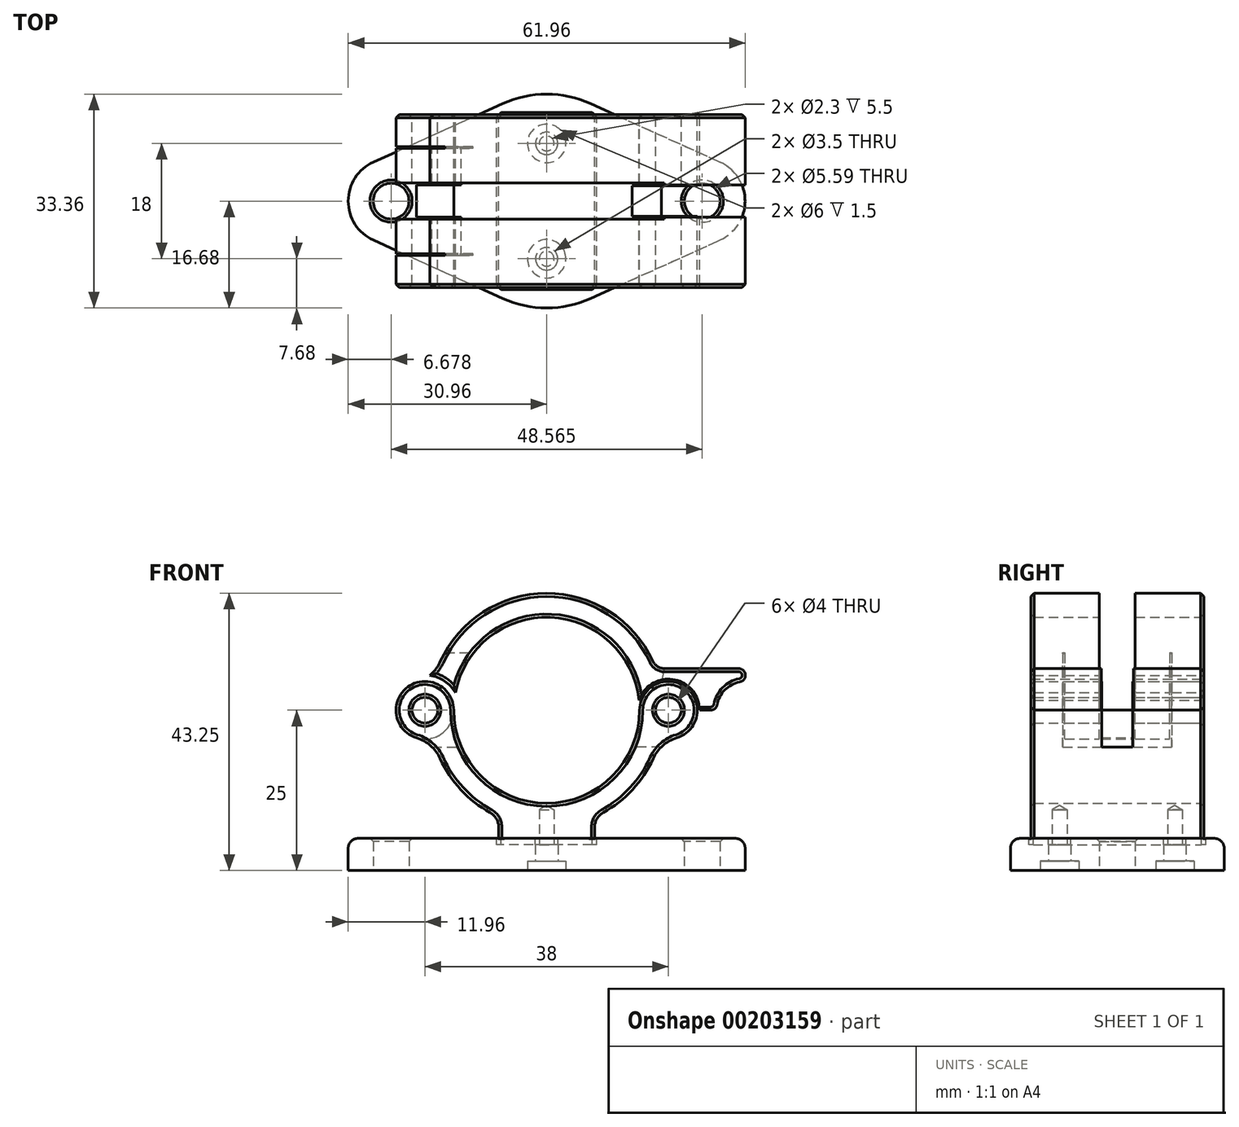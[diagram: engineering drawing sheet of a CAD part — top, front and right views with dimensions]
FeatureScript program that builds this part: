
annotation { "Feature Type Name" : "Feature", "Feature Type Description" : "" }
export const myFeature = defineFeature(function(context is Context, id is Id, definition is map)
    precondition{}
    {
        {
            var Q0;
            Q0=qCreatedBy(makeId("Top.planeOp"),FACE);
            cPlane(context, id + "F0", {"entities" : qUnion([Q0]), "cplaneType" : CPlaneType.OFFSET, "offset" : 30 * mm, "width" : 150 * mm, "height" : 150 * mm});
        }
        {
            var Q0;
            Q0=qCreatedBy(makeId("Top.planeOp"),FACE);
            cPlane(context, id + "F1", {"entities" : qUnion([Q0]), "cplaneType" : CPlaneType.OFFSET, "offset" : 4 * mm, "oppositeDirection" : true, "width" : 150 * mm, "height" : 150 * mm});
        }
        {
            var Q0;
            Q0=qCreatedBy(makeId("Front.planeOp"),FACE);
            var sketch = newSketch(context, id + "F2", { "sketchPlane" : qUnion([Q0])});
            skArc(sketch, "E0", {"start": v(14.41, 22.58) * mm, "mid": v(-14.48, 20.2) * mm, "end": v(14.5, 21) * mm});
            skArc(sketch, "E1", {"start": v(8.8, 5) * mm, "mid": v(13.39, 8.6) * mm, "end": v(16.61, 13.44) * mm});
            skLineSegment(sketch, "E2.bottom", {"start": v(7.5, 0) * mm, "end": v(-7.5, 0) * mm});
            skLineSegment(sketch, "E2.left", {"start": v(7.5, 0) * mm, "end": v(7.5, 2.82) * mm});
            skLineSegment(sketch, "E2.right", {"start": v(-7.5, 0) * mm, "end": v(-7.5, 2.82) * mm});
            skPoint(sketch, "E3.visualSharp", {"position": v(-7.5, 4.36) * mm});
            skArc(sketch, "E3.filletArc", {"start": v(-7.5, 2.82) * mm, "mid": v(-7.85, 4.1) * mm, "end": v(-8.8, 5) * mm});
            skPoint(sketch, "E4.visualSharp", {"position": v(7.5, 4.36) * mm});
            skArc(sketch, "E4.filletArc", {"start": v(8.8, 5) * mm, "mid": v(7.85, 4.1) * mm, "end": v(7.5, 2.82) * mm});
            skCircle(sketch, "E5", {"center": v(-19, 21) * mm, "radius": 4.5 * mm});
            skCircle(sketch, "E6", {"center": v(19, 21) * mm, "radius": 4.5 * mm});
            skArc(sketch, "E7.trimOffspring", {"start": v(-16.61, 13.44) * mm, "mid": v(-13.39, 8.6) * mm, "end": v(-8.8, 5) * mm});
            skArc(sketch, "E8.trimOffspring", {"start": v(16.56, 28.66) * mm, "mid": v(-0.06, 39.25) * mm, "end": v(-16.61, 28.56) * mm});
            skCircle(sketch, "E9", {"center": v(-19, 21) * mm, "radius": 2 * mm});
            skCircle(sketch, "E10", {"center": v(19, 21) * mm, "radius": 2 * mm});
            skArc(sketch, "E11", {"start": v(-20.32, 16.7) * mm, "mid": v(-18.12, 15.47) * mm, "end": v(-16.61, 13.44) * mm});
            skArc(sketch, "E12", {"start": v(16.61, 13.44) * mm, "mid": v(18.12, 15.47) * mm, "end": v(20.32, 16.7) * mm});
            skArc(sketch, "E13", {"start": v(-20.32, 25.3) * mm, "mid": v(-18.12, 26.53) * mm, "end": v(-16.61, 28.56) * mm});
            skArc(sketch, "E14", {"start": v(14.41, 22.58) * mm, "mid": v(19.8, 25.78) * mm, "end": v(23.85, 21) * mm});
            skLineSegment(sketch, "E15", {"start": v(18.38, 27.5) * mm, "end": v(29.95, 27.5) * mm});
            skArc(sketch, "E16.filletArc", {"start": v(16.56, 28.66) * mm, "mid": v(17.3, 27.81) * mm, "end": v(18.38, 27.5) * mm});
            skLineSegment(sketch, "E17", {"start": v(23.85, 21) * mm, "end": v(25.6, 21) * mm});
            skPoint(sketch, "E18.visualSharp", {"position": v(26.5, 21) * mm});
            skArc(sketch, "E18.filletArc", {"start": v(25.6, 21) * mm, "mid": v(26.23, 21.23) * mm, "end": v(26.58, 21.82) * mm});
            skArc(sketch, "E19", {"start": v(30.15, 25.42) * mm, "mid": v(27.8, 24.17) * mm, "end": v(26.58, 21.82) * mm});
            skPoint(sketch, "E20.orphan", {"position": v(14.15, 21) * mm});
            skArc(sketch, "E21", {"start": v(30.15, 25.42) * mm, "mid": v(31, 26.55) * mm, "end": v(29.95, 27.5) * mm});
            skPoint(sketch, "E22.orphan", {"position": v(31, 25.5) * mm});
            skLineSegment(sketch, "E23", {"start": v(19, 21) * mm, "end": v(19, 36.48) * mm, "construction": true});
            skArc(sketch, "E24", {"start": v(-18.22, 26.44) * mm, "mid": v(-15.92, 25.55) * mm, "end": v(-14.24, 23.75) * mm});
            skLineSegment(sketch, "E25", {"start": v(18.38, 27.5) * mm, "end": v(17.05, 21.43) * mm});
            skSolve(sketch);
        }
        {
            var Q0;
            Q0=qCreatedBy(id+"F1.planeOp",FACE);
            var sketch = newSketch(context, id + "F3", { "sketchPlane" : qUnion([Q0])});
            skLineSegment(sketch, "E26", {"start": v(-36.59, 0) * mm, "end": v(35.35, 0) * mm, "construction": true});
            skCircle(sketch, "E27", {"center": v(-24.28, 0) * mm, "radius": 2.8 * mm});
            skArc(sketch, "E28", {"start": v(-27.03, 6.09) * mm, "mid": v(-30.96, 0) * mm, "end": v(-27.03, -6.09) * mm});
            skCircle(sketch, "E29", {"center": v(24.28, 0) * mm, "radius": 2.8 * mm});
            skArc(sketch, "E30", {"start": v(27.03, -6.09) * mm, "mid": v(30.96, 0) * mm, "end": v(27.03, 6.09) * mm});
            skArc(sketch, "E31", {"start": v(-6.86, -15.2) * mm, "mid": v(0, -16.68) * mm, "end": v(6.86, -15.2) * mm});
            skLineSegment(sketch, "E32", {"start": v(-27.03, 6.09) * mm, "end": v(-6.86, 15.2) * mm});
            skLineSegment(sketch, "E33", {"start": v(6.86, -15.2) * mm, "end": v(27.03, -6.09) * mm});
            skLineSegment(sketch, "E34", {"start": v(6.86, 15.2) * mm, "end": v(28.73, 5.32) * mm});
            skLineSegment(sketch, "E35", {"start": v(-27.03, -6.09) * mm, "end": v(-6.86, -15.2) * mm});
            skArc(sketch, "E36.trimOffspring", {"start": v(6.86, 15.2) * mm, "mid": v(0, 16.68) * mm, "end": v(-6.86, 15.2) * mm});
            skLineSegment(sketch, "E37.bottom", {"start": v(5.7, -13.5) * mm, "end": v(-7.5, -13.5) * mm, "construction": true});
            skLineSegment(sketch, "E37.top", {"start": v(7.5, 13.5) * mm, "end": v(-5.7, 13.5) * mm, "construction": true});
            skLineSegment(sketch, "E38", {"start": v(0, -16.68) * mm, "end": v(0, 16.68) * mm, "construction": true});
            skPoint(sketch, "E39", {"position": v(0, -9) * mm});
            skPoint(sketch, "E40", {"position": v(0, 9) * mm});
            skSolve(sketch);
        }
        {
            var Q0;
            Q0=makeQuery(id+"F3.imprint","IMPRINT",FACE,{"disambiguationData":[TD([[makeQuery(id+"F3.imprint","IMPRINT",EDGE,{"derivedFrom":sQuery(id+"F3.wireOp",EDGE,"E27")}),-1.0]])]});
            extrude(context, id + "F4", {"entities" : qUnion([Q0]), "depth" : 5 * mm});
        }
        {
            var Q0;
            Q0=makeQuery(id+"F2.imprint","IMPRINT",FACE,{"disambiguationData":[TD([[makeQuery(id+"F2.imprint","IMPRINT",EDGE,{"derivedFrom":sQuery(id+"F2.wireOp",EDGE,"E1")}),1.0]])]});
            var Q1;
            Q1=makeQuery(id+"F2.imprint","IMPRINT",FACE,{"disambiguationData":[TD([[makeQuery(id+"F2.imprint","IMPRINT",EDGE,{"derivedFrom":sQuery(id+"F2.wireOp",EDGE,"E10")}),-1.0]])]});
            var Q2;
            Q2=makeQuery(id+"F2.imprint","IMPRINT",FACE,{"disambiguationData":[TD([[makeQuery(id+"F2.imprint","IMPRINT",EDGE,{"derivedFrom":sQuery(id+"F2.wireOp",EDGE,"E9")}),-1.0]])]});
            extrude(context, id + "F5", {"entities" : qUnion([Q0, Q1, Q2]), "endBound" : BoundingType.SYMMETRIC, "depth" : 27 * mm});
        }
        {
            var Q0;
            Q0=makeQuery(id+"F2.imprint","IMPRINT",FACE,{"disambiguationData":[TD([[makeQuery(id+"F2.imprint","IMPRINT",EDGE,{"derivedFrom":sQuery(id+"F2.wireOp",EDGE,"E8.trimOffspring")}),1.0]])]});
            var Q1;
            {var subQ1=sQuery(id+"F2.wireOp",EDGE,"E15");Q1=makeQuery(id+"F2.imprint","IMPRINT",FACE,{"disambiguationData":[TD([[makeQuery(id+"F2.imprint","IMPRINT",EDGE,{"derivedFrom":subQ1}),-1.0]])]});}
            extrude(context, id + "F6", {"entities" : qUnion([Q0, Q1]), "endBound" : BoundingType.SYMMETRIC, "depth" : 27 * mm});
        }
        {
            var Q0;
            Q0=sQuery(id+"F3.wireOp",VERTEX,"E40");
            var Q1;
            Q1=sQuery(id+"F3.wireOp",VERTEX,"E39");
            var Q2;
            Q2=makeQuery(id+"F4.opExtrude","SWEPT_BODY",BODY,{"disambiguationData":[OSD([sQuery(id+"F3.wireOp",EDGE,"E27"),sQuery(id+"F3.wireOp",EDGE,"E28"),sQuery(id+"F3.wireOp",EDGE,"E29"),sQuery(id+"F3.wireOp",EDGE,"E30"),sQuery(id+"F3.wireOp",EDGE,"E31"),sQuery(id+"F3.wireOp",EDGE,"E32"),sQuery(id+"F3.wireOp",EDGE,"E33"),sQuery(id+"F3.wireOp",EDGE,"E34"),sQuery(id+"F3.wireOp",EDGE,"E35"),sQuery(id+"F3.wireOp",EDGE,"E36.trimOffspring")])]});
            hole(context, id + "F7", {"style" : HoleStyle.C_BORE, "endStyle" : HoleEndStyle.THROUGH, "oppositeDirection" : true, "holeDiameter" : 3.5 * mm, "cBoreDiameter" : 6 * mm, "cBoreDepth" : 1.5 * mm, "startFromSketch" : true, "locations" : qUnion([Q0, Q1]), "scope" : qUnion([Q2]), "isTappedThrough" : true});
        }
        {
            var Q0;
            Q0=sQuery(id+"F3.wireOp",VERTEX,"E39");
            var Q1;
            Q1=sQuery(id+"F3.wireOp",VERTEX,"E40");
            var Q2;
            Q2=makeQuery(id+"F5.opExtrude","SWEPT_BODY",BODY,{"disambiguationData":[OSD([sQuery(id+"F2.wireOp",EDGE,"E0"),sQuery(id+"F2.wireOp",EDGE,"E1"),sQuery(id+"F2.wireOp",EDGE,"E2.bottom"),sQuery(id+"F2.wireOp",EDGE,"E2.left"),sQuery(id+"F2.wireOp",EDGE,"E2.right"),sQuery(id+"F2.wireOp",EDGE,"E3.filletArc"),sQuery(id+"F2.wireOp",EDGE,"E4.filletArc"),sQuery(id+"F2.wireOp",EDGE,"E5"),sQuery(id+"F2.wireOp",EDGE,"E6"),sQuery(id+"F2.wireOp",EDGE,"E7.trimOffspring"),sQuery(id+"F2.wireOp",EDGE,"E9"),sQuery(id+"F2.wireOp",EDGE,"E10"),sQuery(id+"F2.wireOp",EDGE,"E11"),sQuery(id+"F2.wireOp",EDGE,"E12")])]});
            hole(context, id + "F8", {"style" : HoleStyle.SIMPLE, "endStyle" : HoleEndStyle.BLIND, "oppositeDirection" : true, "holeDiameter" : 2.3 * mm, "holeDepth" : 9.5 * mm, "startFromSketch" : true, "locations" : qUnion([Q0, Q1]), "scope" : qUnion([Q2])});
        }
        {
            var Q0;
            Q0=qCreatedBy(id+"F0.planeOp",FACE);
            var sketch = newSketch(context, id + "F9", { "sketchPlane" : qUnion([Q0])});
            skLineSegment(sketch, "E41.0", {"start": v(23.5, -13.5) * mm, "end": v(14.5, -13.5) * mm});
            skLineSegment(sketch, "E42.0", {"start": v(23.5, 13.5) * mm, "end": v(14.5, 13.5) * mm});
            skLineSegment(sketch, "E43", {"start": v(23.5, 13.5) * mm, "end": v(23.5, -13.5) * mm});
            skLineSegment(sketch, "E44", {"start": v(-23.5, -13.5) * mm, "end": v(-23.5, 13.5) * mm});
            skLineSegment(sketch, "E45.0", {"start": v(-14.5, -13.5) * mm, "end": v(-23.5, -13.5) * mm});
            skLineSegment(sketch, "E46.bottom", {"start": v(-23.5, 2.5) * mm, "end": v(-11.5, 2.5) * mm});
            skLineSegment(sketch, "E46.top", {"start": v(-23.5, 8.5) * mm, "end": v(-11.5, 8.5) * mm});
            skLineSegment(sketch, "E46.left", {"start": v(-23.5, 2.5) * mm, "end": v(-23.5, 8.5) * mm});
            skLineSegment(sketch, "E46.right", {"start": v(-11.5, 2.5) * mm, "end": v(-11.5, 8.5) * mm});
            skLineSegment(sketch, "E47.bottom", {"start": v(-23.5, -2.5) * mm, "end": v(-11.5, -2.5) * mm});
            skLineSegment(sketch, "E47.top", {"start": v(-23.5, -8.5) * mm, "end": v(-11.5, -8.5) * mm});
            skLineSegment(sketch, "E47.left", {"start": v(-23.5, -2.5) * mm, "end": v(-23.5, -8.5) * mm});
            skLineSegment(sketch, "E47.right", {"start": v(-11.5, -2.5) * mm, "end": v(-11.5, -8.5) * mm});
            skLineSegment(sketch, "E48.bottom", {"start": v(23.5, 2.4) * mm, "end": v(11.5, 2.4) * mm});
            skLineSegment(sketch, "E48.top", {"start": v(23.5, -2.4) * mm, "end": v(11.5, -2.4) * mm});
            skLineSegment(sketch, "E48.left", {"start": v(23.5, 2.4) * mm, "end": v(23.5, -2.4) * mm});
            skLineSegment(sketch, "E48.right", {"start": v(11.5, 2.4) * mm, "end": v(11.5, -2.4) * mm});
            skSolve(sketch);
        }
        {
            var Q0;
            Q0=makeQuery(id+"F9.imprint","IMPRINT",FACE,{"disambiguationData":[TD([[makeQuery(id+"F9.imprint","IMPRINT",EDGE,{"derivedFrom":sQuery(id+"F9.wireOp",EDGE,"E46.bottom")}),1.0]])]});
            var Q1;
            Q1=makeQuery(id+"F9.imprint","IMPRINT",FACE,{"disambiguationData":[TD([[makeQuery(id+"F9.imprint","IMPRINT",EDGE,{"derivedFrom":sQuery(id+"F9.wireOp",EDGE,"E47.bottom")}),-1.0]])]});
            var Q2;
            Q2=makeQuery(id+"F9.imprint","IMPRINT",FACE,{"disambiguationData":[TD([[makeQuery(id+"F9.imprint","IMPRINT",EDGE,{"derivedFrom":sQuery(id+"F9.wireOp",EDGE,"E48.bottom")}),1.0]])]});
            extrude(context, id + "F10", {"entities" : qUnion([Q0, Q1, Q2]), "operationType" : NewBodyOperationType.REMOVE, "oppositeDirection" : true, "depth" : 14.75 * mm});
        }
        {
            var Q0;
            Q0=makeQuery(id+"F2.imprint","IMPRINT",FACE,{"disambiguationData":[TD([[makeQuery(id+"F2.imprint","IMPRINT",EDGE,{"derivedFrom":sQuery(id+"F2.wireOp",EDGE,"E9")}),-1.0]])]});
            var Q1;
            {var subQ0=sQuery(id+"F2.wireOp",EDGE,"E24");Q1=makeQuery(id+"F2.imprint","IMPRINT",FACE,{"disambiguationData":[TD([[makeQuery(id+"F2.imprint","IMPRINT",EDGE,{"derivedFrom":subQ0}),-1.0]])]});}
            extrude(context, id + "F11", {"entities" : qUnion([Q0, Q1]), "operationType" : NewBodyOperationType.ADD, "endBound" : BoundingType.SYMMETRIC, "depth" : 16.4 * mm});
        }
        {
            var Q0;
            Q0=makeQuery(id+"F2.imprint","IMPRINT",FACE,{"disambiguationData":[TD([[makeQuery(id+"F2.imprint","IMPRINT",EDGE,{"derivedFrom":sQuery(id+"F2.wireOp",EDGE,"E9")}),-1.0]])]});
            var Q1;
            {var subQ0=sQuery(id+"F2.wireOp",EDGE,"E24");Q1=makeQuery(id+"F2.imprint","IMPRINT",FACE,{"disambiguationData":[TD([[makeQuery(id+"F2.imprint","IMPRINT",EDGE,{"derivedFrom":subQ0}),-1.0]])]});}
            extrude(context, id + "F12", {"entities" : qUnion([Q0, Q1]), "operationType" : NewBodyOperationType.REMOVE, "endBound" : BoundingType.SYMMETRIC, "depth" : 5.6 * mm});
        }
        {
            var Q0;
            {var subQ1=sQuery(id+"F2.wireOp",EDGE,"E15");Q0=makeQuery(id+"F2.imprint","IMPRINT",FACE,{"disambiguationData":[TD([[makeQuery(id+"F2.imprint","IMPRINT",EDGE,{"derivedFrom":subQ1}),-1.0]])]});}
            extrude(context, id + "F13", {"entities" : qUnion([Q0]), "operationType" : NewBodyOperationType.REMOVE, "endBound" : BoundingType.SYMMETRIC, "depth" : 5 * mm});
        }
        {
            var Q0;
            Q0=makeQuery(id+"F6.opExtrude","CAP_EDGE",EDGE,{"disambiguationData":[OSD([sQuery(id+"F2.wireOp",EDGE,"E8.trimOffspring")])],"isStart":false});
            var Q1;
            Q1=makeQuery(id+"F5.opExtrude","CAP_EDGE",EDGE,{"disambiguationData":[OSD([sQuery(id+"F2.wireOp",EDGE,"E0")])],"isStart":false});
            var Q2;
            Q2=makeQuery(id+"F6.opExtrude","CAP_EDGE",EDGE,{"disambiguationData":[OSD([sQuery(id+"F2.wireOp",EDGE,"E0")])],"isStart":false});
            var Q3;
            Q3=makeQuery(id+"F6.opExtrude","CAP_EDGE",EDGE,{"disambiguationData":[OSD([sQuery(id+"F2.wireOp",EDGE,"E24")])],"isStart":false});
            var Q4;
            Q4=makeQuery(id+"F6.opExtrude","CAP_EDGE",EDGE,{"disambiguationData":[OSD([sQuery(id+"F2.wireOp",EDGE,"E0")])],"isStart":true});
            var Q5;
            Q5=makeQuery(id+"F6.opExtrude","CAP_EDGE",EDGE,{"disambiguationData":[OSD([sQuery(id+"F2.wireOp",EDGE,"E8.trimOffspring")])],"isStart":true});
            var Q6;
            Q6=makeQuery(id+"F5.opExtrude","CAP_EDGE",EDGE,{"disambiguationData":[OSD([sQuery(id+"F2.wireOp",EDGE,"E0")])],"isStart":true});
            var Q7;
            Q7=makeQuery(id+"F5.opExtrude","CAP_EDGE",EDGE,{"disambiguationData":[OSD([sQuery(id+"F2.wireOp",EDGE,"E7.trimOffspring")])],"isStart":true});
            var Q8;
            Q8=makeQuery(id+"F4.opExtrude","CAP_EDGE",EDGE,{"disambiguationData":[OSD([sQuery(id+"F3.wireOp",EDGE,"E29")])],"isStart":false});
            var Q9;
            Q9=makeQuery(id+"F4.opExtrude","CAP_EDGE",EDGE,{"disambiguationData":[OSD([sQuery(id+"F3.wireOp",EDGE,"E27")])],"isStart":false});
            var Q10;
            Q10=makeQuery(id+"F7.hole-0.boolean.opBoolean","COPY",EDGE,{"derivedFrom":makeQuery(id+"F7.hole-0.opRevolve","SWEPT_EDGE",EDGE,{"disambiguationData":[OSD([sQuery(id+"F7.hole-0.sketch.wireOp",EDGE,"cbore_start_line_2"),sQuery(id+"F7.hole-0.sketch.wireOp",EDGE,"cbore_start_line_3")])]})});
            var Q11;
            Q11=makeQuery(id+"F7.hole-1.boolean.opBoolean","COPY",EDGE,{"derivedFrom":makeQuery(id+"F7.hole-1.opRevolve","SWEPT_EDGE",EDGE,{"disambiguationData":[OSD([sQuery(id+"F7.hole-1.sketch.wireOp",EDGE,"cbore_start_line_2"),sQuery(id+"F7.hole-1.sketch.wireOp",EDGE,"cbore_start_line_3")])]})});
            var Q12;
            Q12=makeQuery(id+"F8.hole-1.boolean.opBoolean","INTERSECT",EDGE,{"derivedFrom":[makeQuery(id+"F5.opExtrude","SWEPT_FACE",FACE,{"disambiguationData":[OSD([sQuery(id+"F2.wireOp",EDGE,"E2.bottom")])]}),makeQuery(id+"F8.hole-1.opRevolve","SWEPT_FACE",FACE,{"disambiguationData":[OSD([sQuery(id+"F8.hole-1.sketch.wireOp",EDGE,"core_line_2")])]})]});
            var Q13;
            Q13=makeQuery(id+"F8.hole-0.boolean.opBoolean","INTERSECT",EDGE,{"derivedFrom":[makeQuery(id+"F5.opExtrude","SWEPT_FACE",FACE,{"disambiguationData":[OSD([sQuery(id+"F2.wireOp",EDGE,"E2.bottom")])]}),makeQuery(id+"F8.hole-0.opRevolve","SWEPT_FACE",FACE,{"disambiguationData":[OSD([sQuery(id+"F8.hole-0.sketch.wireOp",EDGE,"core_line_2")])]})]});
            var Q14;
            Q14=makeQuery(id+"F5.opExtrude","CAP_EDGE",EDGE,{"disambiguationData":[OSD([sQuery(id+"F2.wireOp",EDGE,"E9")])],"isStart":true});
            var Q15;
            Q15=makeQuery(id+"F5.opExtrude","CAP_EDGE",EDGE,{"disambiguationData":[OSD([sQuery(id+"F2.wireOp",EDGE,"E10")])],"isStart":true});
            var Q16;
            Q16=makeQuery(id+"F5.opExtrude","CAP_EDGE",EDGE,{"disambiguationData":[OSD([sQuery(id+"F2.wireOp",EDGE,"E9")])],"isStart":false});
            var Q17;
            Q17=makeQuery(id+"F5.opExtrude","CAP_EDGE",EDGE,{"disambiguationData":[OSD([sQuery(id+"F2.wireOp",EDGE,"E10")])],"isStart":false});
            chamfer(context, id + "F14", {"entities" : qUnion([Q0, Q1, Q2, Q3, Q4, Q5, Q6, Q7, Q8, Q9, Q10, Q11, Q12, Q13, Q14, Q15, Q16, Q17]), "width" : .5 * mm, "tangentPropagation" : true});
        }
        {
            var Q0;
            Q0=makeQuery(id+"F4.opExtrude","CAP_FACE",FACE,{"disambiguationData":[OSD([sQuery(id+"F3.wireOp",EDGE,"E27"),sQuery(id+"F3.wireOp",EDGE,"E28"),sQuery(id+"F3.wireOp",EDGE,"E29"),sQuery(id+"F3.wireOp",EDGE,"E30"),sQuery(id+"F3.wireOp",EDGE,"E31"),sQuery(id+"F3.wireOp",EDGE,"E32"),sQuery(id+"F3.wireOp",EDGE,"E33"),sQuery(id+"F3.wireOp",EDGE,"E34"),sQuery(id+"F3.wireOp",EDGE,"E35"),sQuery(id+"F3.wireOp",EDGE,"E36.trimOffspring")])],"isStart":false});
            var sketch = newSketch(context, id + "F15", { "sketchPlane" : qUnion([Q0])});
            skLineSegment(sketch, "E49.0", {"start": v(7, 13.5) * mm, "end": v(-7, 13.5) * mm});
            skLineSegment(sketch, "E50.0", {"start": v(7.5, -13) * mm, "end": v(7.5, 13) * mm});
            skLineSegment(sketch, "E51.0", {"start": v(-7.5, -13) * mm, "end": v(-7.5, 13) * mm});
            skLineSegment(sketch, "E52.0", {"start": v(7, -13.5) * mm, "end": v(-7, -13.5) * mm});
            skLineSegment(sketch, "E53.0", {"start": v(7.5, -13) * mm, "end": v(7, -13.5) * mm});
            skLineSegment(sketch, "E54.0", {"start": v(-7, -13.5) * mm, "end": v(-7.5, -13) * mm});
            skLineSegment(sketch, "E55.0", {"start": v(-7, 13.5) * mm, "end": v(-7.5, 13) * mm});
            skLineSegment(sketch, "E56.0", {"start": v(7, 13.5) * mm, "end": v(7.5, 13) * mm});
            skLineSegment(sketch, "E57.0", {"start": v(-7.12, -13.8) * mm, "end": v(-7.8, -13.12) * mm});
            skLineSegment(sketch, "E57.1", {"start": v(7.12, -13.8) * mm, "end": v(-7.12, -13.8) * mm});
            skLineSegment(sketch, "E57.2", {"start": v(-7.8, -13.12) * mm, "end": v(-7.8, 13.12) * mm});
            skLineSegment(sketch, "E57.3", {"start": v(7.8, -13.12) * mm, "end": v(7.12, -13.8) * mm});
            skLineSegment(sketch, "E57.4", {"start": v(-7.12, 13.8) * mm, "end": v(-7.8, 13.12) * mm});
            skLineSegment(sketch, "E57.5", {"start": v(7.12, 13.8) * mm, "end": v(-7.12, 13.8) * mm});
            skLineSegment(sketch, "E57.6", {"start": v(7.12, 13.8) * mm, "end": v(7.8, 13.12) * mm});
            skLineSegment(sketch, "E57.7", {"start": v(7.8, -13.12) * mm, "end": v(7.8, 13.12) * mm});
            skArc(sketch, "E58.0", {"start": v(4.8, 10.64) * mm, "mid": v(0, 11.68) * mm, "end": v(-4.8, 10.64) * mm});
            skLineSegment(sketch, "E58.1", {"start": v(24.97, 1.53) * mm, "end": v(4.8, 10.64) * mm});
            skLineSegment(sketch, "E58.2", {"start": v(-4.8, 10.64) * mm, "end": v(-24.97, 1.53) * mm});
            skArc(sketch, "E58.3", {"start": v(24.97, -1.53) * mm, "mid": v(25.96, 0) * mm, "end": v(24.97, 1.53) * mm});
            skArc(sketch, "E58.4", {"start": v(-24.97, 1.53) * mm, "mid": v(-25.96, 0) * mm, "end": v(-24.97, -1.53) * mm});
            skLineSegment(sketch, "E58.5", {"start": v(-24.97, -1.53) * mm, "end": v(-4.8, -10.64) * mm});
            skArc(sketch, "E58.6", {"start": v(-4.8, -10.64) * mm, "mid": v(0, -11.68) * mm, "end": v(4.8, -10.64) * mm});
            skLineSegment(sketch, "E58.7", {"start": v(4.8, -10.64) * mm, "end": v(24.97, -1.53) * mm});
            skSolve(sketch);
        }
        {
            var Q0;
            Q0=makeQuery(id+"F15.imprint","IMPRINT",FACE,{"disambiguationData":[TD([[makeQuery(id+"F15.imprint","IMPRINT",EDGE,{"derivedFrom":sQuery(id+"F15.wireOp",EDGE,"E49.0")}),1.0]])]});
            var Q1;
            {var subQ0=sQuery(id+"F15.wireOp",EDGE,"E58.0");Q1=makeQuery(id+"F15.imprint","IMPRINT",FACE,{"disambiguationData":[TD([[makeQuery(id+"F15.imprint","IMPRINT",EDGE,{"derivedFrom":subQ0}),1.0]])]});}
            var Q2;
            {var subQ0=sQuery(id+"F15.wireOp",EDGE,"E58.7");var subQ1=sQuery(id+"F15.wireOp",EDGE,"E50.0");var subQ2=makeQuery(id+"F15.imprint","INTERSECT",VERTEX,{"derivedFrom":[subQ1,subQ0]});Q2=makeQuery(id+"F15.imprint","IMPRINT",FACE,{"disambiguationData":[TD([[makeQuery(id+"F15.imprint","IMPRINT",EDGE,{"disambiguationData":[TD([[subQ2,-1.0]])],"derivedFrom":subQ1}),-1.0]])]});}
            var Q3;
            Q3=makeQuery(id+"F15.imprint","IMPRINT",FACE,{"disambiguationData":[TD([[makeQuery(id+"F15.imprint","IMPRINT",EDGE,{"derivedFrom":sQuery(id+"F15.wireOp",EDGE,"E52.0")}),-1.0]])]});
            var Q4;
            {var subQ0=sQuery(id+"F15.wireOp",EDGE,"E58.5");var subQ1=sQuery(id+"F15.wireOp",EDGE,"E51.0");var subQ2=makeQuery(id+"F15.imprint","INTERSECT",VERTEX,{"derivedFrom":[subQ1,subQ0]});Q4=makeQuery(id+"F15.imprint","IMPRINT",FACE,{"disambiguationData":[TD([[makeQuery(id+"F15.imprint","IMPRINT",EDGE,{"disambiguationData":[TD([[subQ2,-1.0]])],"derivedFrom":subQ1}),1.0]])]});}
            var Q5;
            Q5=makeQuery(id+"F15.imprint","IMPRINT",FACE,{"disambiguationData":[TD([[makeQuery(id+"F15.imprint","IMPRINT",EDGE,{"derivedFrom":sQuery(id+"F15.wireOp",EDGE,"E52.0")}),1.0]])]});
            var Q6;
            Q6=makeQuery(id+"F15.imprint","IMPRINT",FACE,{"disambiguationData":[TD([[makeQuery(id+"F15.imprint","IMPRINT",EDGE,{"derivedFrom":sQuery(id+"F15.wireOp",EDGE,"E49.0")}),-1.0]])]});
            extrude(context, id + "F16", {"entities" : qUnion([Q0, Q1, Q2, Q3, Q4, Q5, Q6]), "operationType" : NewBodyOperationType.REMOVE, "oppositeDirection" : true, "depth" : 1 * mm});
        }
        {
            var Q0;
            Q0=makeQuery(id+"F4.opExtrude","CAP_EDGE",EDGE,{"disambiguationData":[OSD([sQuery(id+"F3.wireOp",EDGE,"E35")])],"isStart":false});
            fillet(context, id + "F17", {"entities" : qUnion([Q0]), "radius" : 1.5 * mm, "tangentPropagation" : true, "allowEdgeOverflow" : false});
        }
    });
